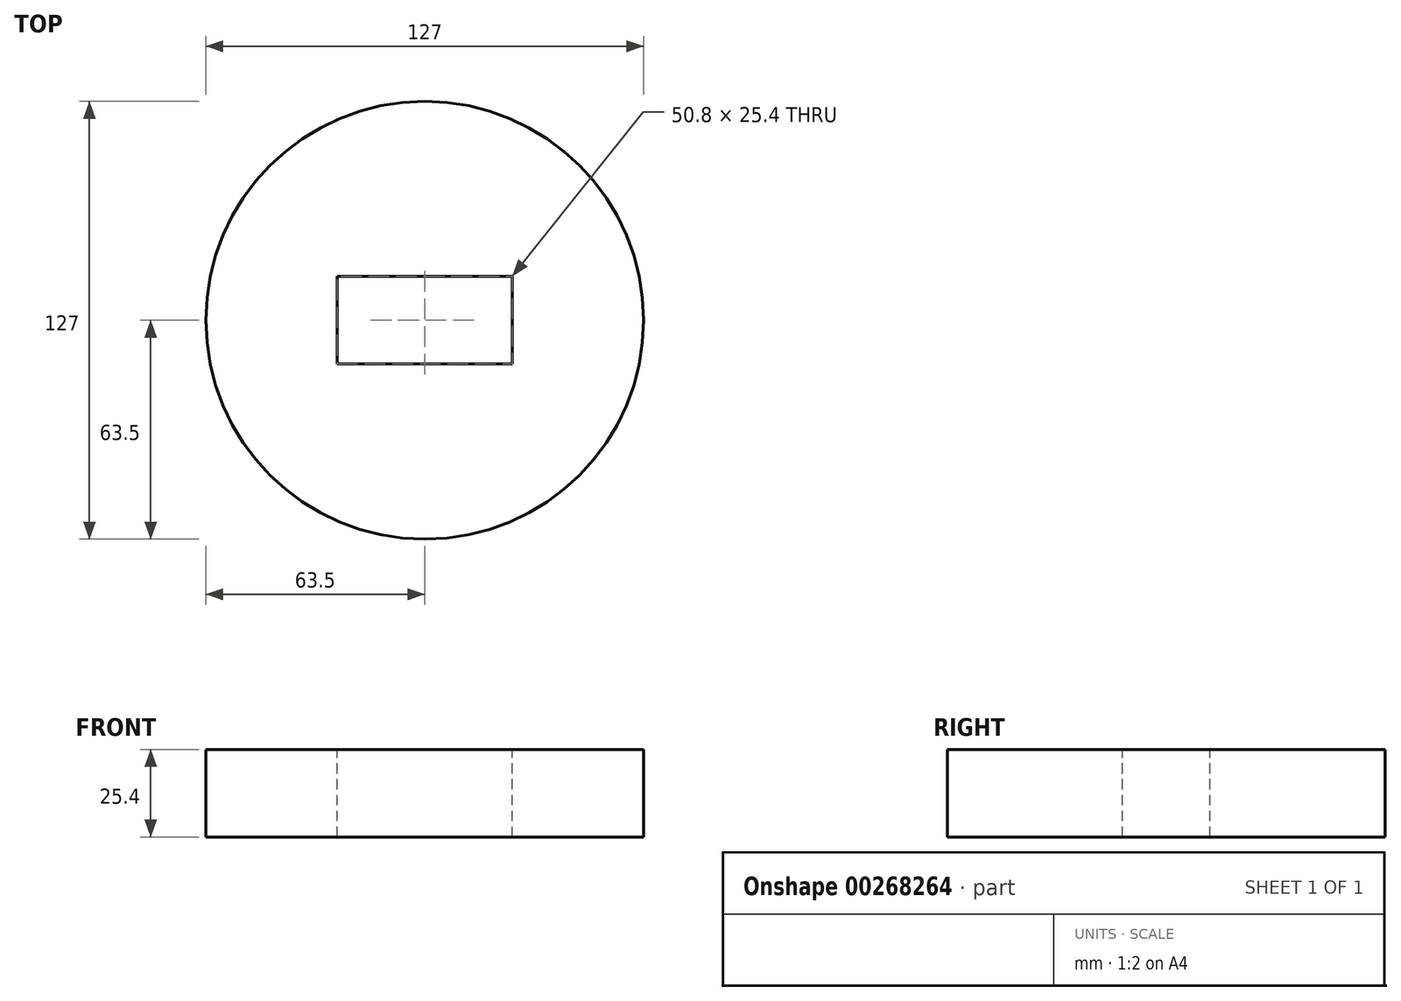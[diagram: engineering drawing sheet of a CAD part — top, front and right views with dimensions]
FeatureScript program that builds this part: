
annotation { "Feature Type Name" : "Feature", "Feature Type Description" : "" }
export const myFeature = defineFeature(function(context is Context, id is Id, definition is map)
    precondition{}
    {
        {
            var Q0;
            Q0=qCreatedBy(makeId("Top.planeOp"),FACE);
            var sketch = newSketch(context, id + "F0", { "sketchPlane" : qUnion([Q0])});
            skCircle(sketch, "E0", {"center": v(0, 0) * mm, "radius": 63.5 * mm});
            skSolve(sketch);
        }
        {
            var Q0;
            Q0=makeQuery(id+"F0.imprint","IMPRINT",FACE,{"disambiguationData":[TD([[makeQuery(id+"F0.imprint","IMPRINT",EDGE,{"derivedFrom":sQuery(id+"F0.wireOp",EDGE,"E0")}),1.0]])]});
            extrude(context, id + "F1", {"entities" : qUnion([Q0]), "oppositeDirection" : true, "depth" : 25.4 * mm});
        }
        {
            var Q0;
            Q0=makeQuery(id+"F1.opExtrude","CAP_FACE",FACE,{"disambiguationData":[OSD([sQuery(id+"F0.wireOp",EDGE,"E0")])],"isStart":true});
            var sketch = newSketch(context, id + "F2", { "sketchPlane" : qUnion([Q0])});
            skLineSegment(sketch, "E1.bottom", {"start": v(25.4, -12.7) * mm, "end": v(-25.4, -12.7) * mm});
            skLineSegment(sketch, "E1.top", {"start": v(25.4, 12.7) * mm, "end": v(-25.4, 12.7) * mm});
            skLineSegment(sketch, "E1.left", {"start": v(25.4, -12.7) * mm, "end": v(25.4, 12.7) * mm});
            skLineSegment(sketch, "E1.right", {"start": v(-25.4, -12.7) * mm, "end": v(-25.4, 12.7) * mm});
            skSolve(sketch);
        }
        {
            var Q0;
            Q0=makeQuery(id+"F2.imprint","IMPRINT",FACE,{"disambiguationData":[TD([[makeQuery(id+"F2.imprint","IMPRINT",EDGE,{"derivedFrom":sQuery(id+"F2.wireOp",EDGE,"E1.bottom")}),-1.0]])]});
            extrude(context, id + "F3", {"entities" : qUnion([Q0]), "operationType" : NewBodyOperationType.REMOVE, "endBound" : BoundingType.THROUGH_ALL, "oppositeDirection" : true, "depth" : 25.4 * mm});
        }
    });
